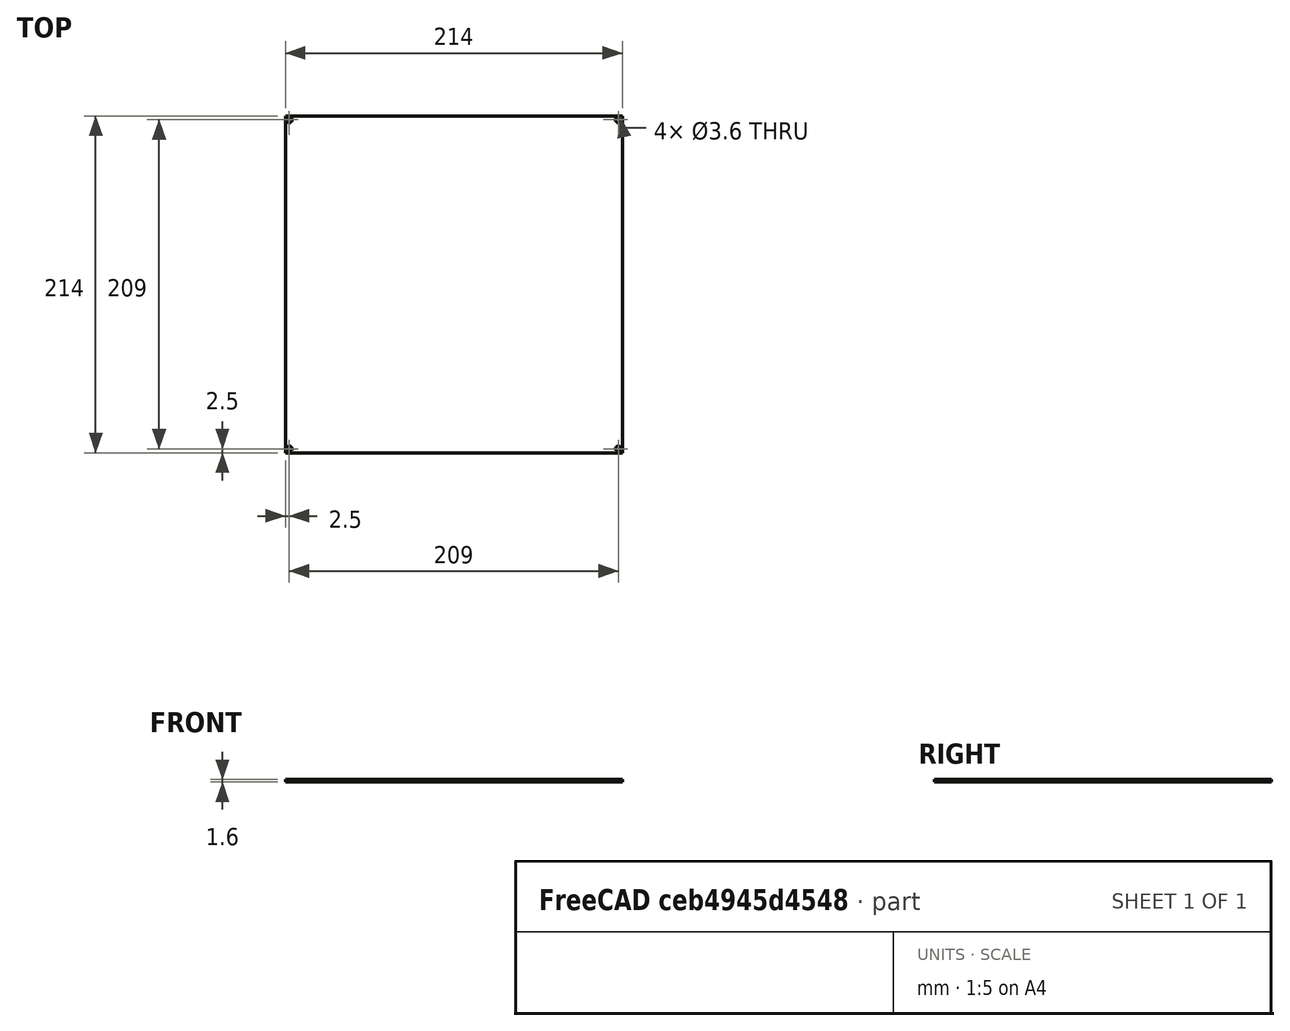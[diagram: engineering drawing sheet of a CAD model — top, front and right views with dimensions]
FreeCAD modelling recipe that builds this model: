
FCSTD DOCUMENT  (FreeCAD 0.16R6706 (Git))
Label: Mesa MK1
License: All rights reserved
LicenseURL: http://en.wikipedia.org/wiki/All_rights_reserved
objects: Sketcher::SketchObject×1, PartDesign::Pad×1
note: 3 computed .brp shape members not serialized (recipe doc carries the construction recipe); baked Part::Feature solids carry a one-line shape summary decoded from their .brp

FEATURE [Sketcher::SketchObject] Sketch
  sketch-geometry (12):
    g0: LineSegment StartX=-107 StartY=107 StartZ=0 EndX=107 EndY=107 EndZ=0
    g1: LineSegment StartX=107 StartY=107 StartZ=0 EndX=107 EndY=-107 EndZ=0
    g2: LineSegment StartX=107 StartY=-107 StartZ=0 EndX=-107 EndY=-107 EndZ=0
    g3: LineSegment StartX=-107 StartY=-107 StartZ=0 EndX=-107 EndY=107 EndZ=0
    g4: LineSegment [constr] StartX=-104.5 StartY=104.5 StartZ=0 EndX=104.5 EndY=104.5 EndZ=0
    g5: LineSegment [constr] StartX=104.5 StartY=104.5 StartZ=0 EndX=104.5 EndY=-104.5 EndZ=0
    g6: LineSegment [constr] StartX=104.5 StartY=-104.5 StartZ=0 EndX=-104.5 EndY=-104.5 EndZ=0
    g7: LineSegment [constr] StartX=-104.5 StartY=-104.5 StartZ=0 EndX=-104.5 EndY=104.5 EndZ=0
    g8: Circle CenterX=-104.5 CenterY=104.5 CenterZ=0 NormalX=0 NormalY=0 NormalZ=1 Radius=1.8
    g9: Circle CenterX=104.5 CenterY=104.5 CenterZ=0 NormalX=0 NormalY=0 NormalZ=1 Radius=1.8
    g10: Circle CenterX=-104.5 CenterY=-104.5 CenterZ=0 NormalX=0 NormalY=0 NormalZ=1 Radius=1.8
    g11: Circle CenterX=104.5 CenterY=-104.5 CenterZ=0 NormalX=0 NormalY=0 NormalZ=1 Radius=1.8
  constraints (30):
    c: Coincident(g0,g1)
    c: Coincident(g1,g2)
    c: Coincident(g2,g3)
    c: Coincident(g3,g0)
    c: Horizontal(g0)
    c: Horizontal(g2)
    c: Vertical(g1)
    c: Vertical(g3)
    c: DistanceX(g0,g0) = 214
    c: Equal(g0,g3)
    c: Symmetric(g0,g2,g-1)
    c: Coincident(g4,g5)
    c: Coincident(g5,g6)
    c: Coincident(g6,g7)
    c: Coincident(g7,g4)
    c: Horizontal(g4)
    c: Horizontal(g6)
    c: Vertical(g5)
    c: Vertical(g7)
    c: Symmetric(g4,g6,g-1)
    c: DistanceX(g4,g4) = 209
    c: Equal(g4,g7)
    c: Radius(g8) = 1.8
    c: Equal(g8,g9) = 1.8
    c: Equal(g8,g10) = 1.8
    c: Equal(g8,g11) = 1.8
    c: Coincident(g4,g8)
    c: Coincident(g6,g10)
    c: Coincident(g4,g9)
    c: Coincident(g5,g11)
FEATURE [PartDesign::Pad] Pad
  Length = 1.6
  Length2 = 100
  Sketch = -> Sketch
  Type = 0
